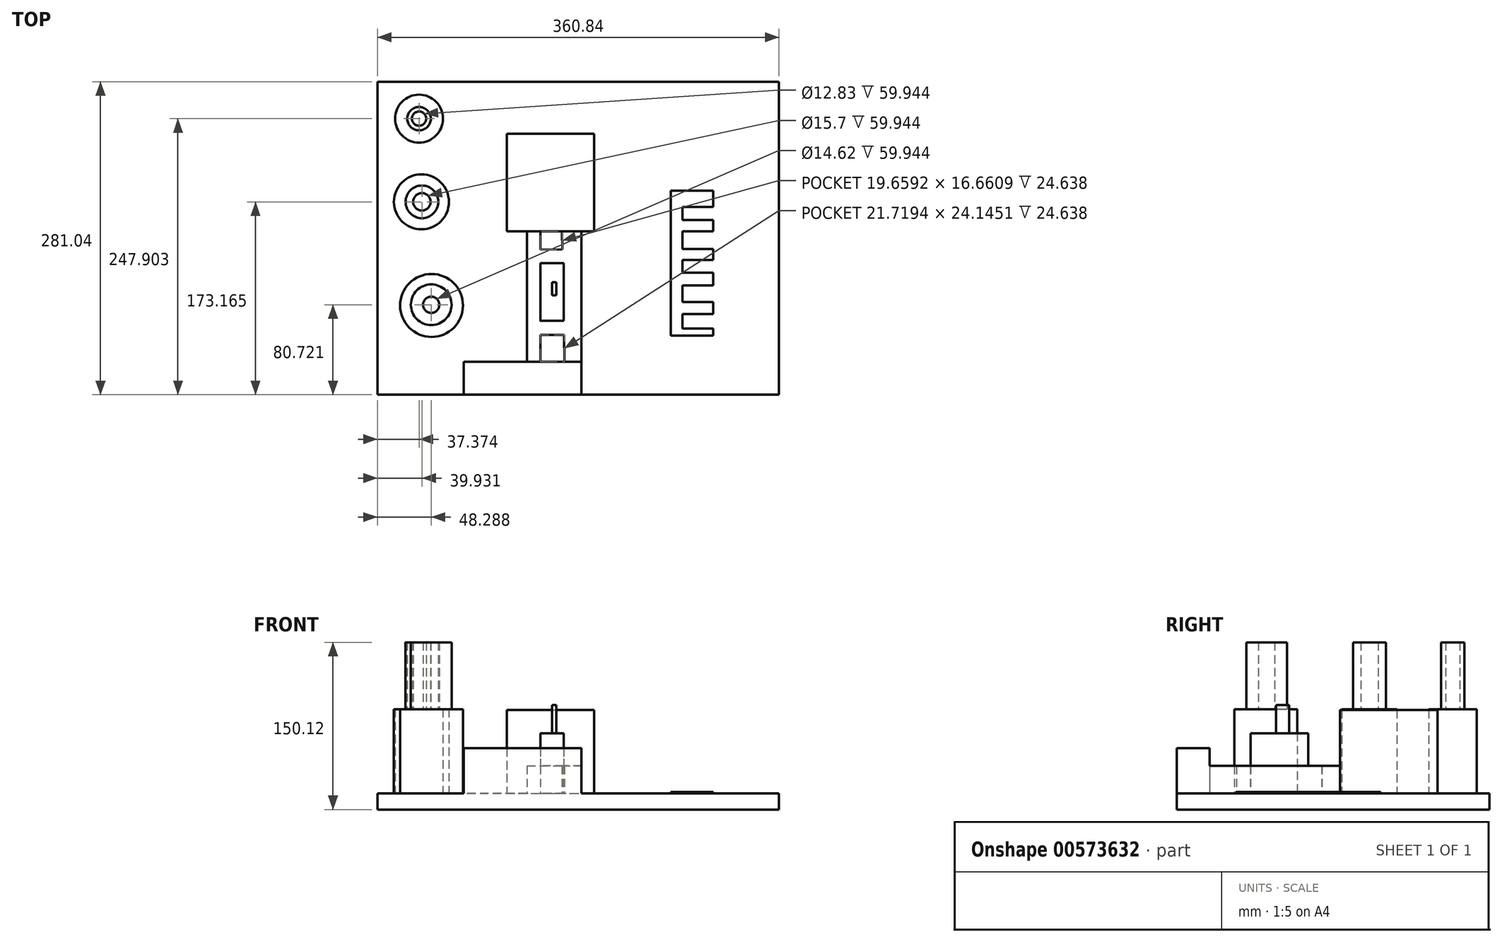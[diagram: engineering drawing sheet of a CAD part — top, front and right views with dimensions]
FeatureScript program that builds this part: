
annotation { "Feature Type Name" : "Feature", "Feature Type Description" : "" }
export const myFeature = defineFeature(function(context is Context, id is Id, definition is map)
    precondition{}
    {
        {
            var Q0;
            Q0=qCreatedBy(makeId("Top.planeOp"),FACE);
            var sketch = newSketch(context, id + "F0", { "sketchPlane" : qUnion([Q0])});
            skLineSegment(sketch, "E0.bottom", {"start": v(-194.6, 134.36) * mm, "end": v(166.24, 134.36) * mm});
            skLineSegment(sketch, "E0.top", {"start": v(-194.6, -146.68) * mm, "end": v(166.24, -146.68) * mm});
            skLineSegment(sketch, "E0.left", {"start": v(-194.6, 134.36) * mm, "end": v(-194.6, -146.68) * mm});
            skLineSegment(sketch, "E0.right", {"start": v(166.24, 134.36) * mm, "end": v(166.24, -146.68) * mm});
            skSolve(sketch);
        }
        {
            var Q0;
            Q0=makeQuery(id+"F0.imprint","IMPRINT",FACE,{"disambiguationData":[TD([[makeQuery(id+"F0.imprint","IMPRINT",EDGE,{"derivedFrom":sQuery(id+"F0.wireOp",EDGE,"E0.bottom")}),-1.0]])]});
            extrude(context, id + "F1", {"entities" : qUnion([Q0]), "oppositeDirection" : true, "depth" : 14.48 * mm, "offsetDistance" : 25.4 * mm});
        }
        {
            var Q0;
            Q0=makeQuery(id+"F1.opExtrude","CAP_FACE",FACE,{"disambiguationData":[OSD([sQuery(id+"F0.wireOp",EDGE,"E0.bottom"),sQuery(id+"F0.wireOp",EDGE,"E0.top"),sQuery(id+"F0.wireOp",EDGE,"E0.left"),sQuery(id+"F0.wireOp",EDGE,"E0.right")])],"isStart":true});
            var sketch = newSketch(context, id + "F2", { "sketchPlane" : qUnion([Q0])});
            skCircle(sketch, "E1", {"center": v(-157.23, 101.22) * mm, "radius": 21.51 * mm});
            skCircle(sketch, "E2", {"center": v(-155.1, 26.46) * mm, "radius": 24.7 * mm});
            skCircle(sketch, "E3", {"center": v(-145.98, -66.55) * mm, "radius": 28.25 * mm});
            skSolve(sketch);
        }
        {
            var Q0;
            Q0 = qSketchRegion(id + "F2", true);
            extrude(context, id + "F3", {"entities" : qUnion([Q0]), "operationType" : NewBodyOperationType.ADD, "depth" : 75.7 * mm, "offsetDistance" : 25.4 * mm});
        }
        {
            var Q0;
            Q0=makeQuery(id+"F3.opExtrude","CAP_FACE",FACE,{"disambiguationData":[OSD([sQuery(id+"F2.wireOp",EDGE,"E1")])],"isStart":false});
            var sketch = newSketch(context, id + "F4", { "sketchPlane" : qUnion([Q0])});
            skCircle(sketch, "E4", {"center": v(-157.23, 101.22) * mm, "radius": 10.56 * mm});
            skCircle(sketch, "E5", {"center": v(-154.67, 26.48) * mm, "radius": 14.66 * mm});
            skCircle(sketch, "E6", {"center": v(-146.31, -65.96) * mm, "radius": 18.29 * mm});
            skCircle(sketch, "E7", {"center": v(-146.31, -65.96) * mm, "radius": 7.31 * mm});
            skCircle(sketch, "E8", {"center": v(-154.67, 26.48) * mm, "radius": 7.85 * mm});
            skCircle(sketch, "E9", {"center": v(-157.23, 101.22) * mm, "radius": 6.41 * mm});
            skSolve(sketch);
        }
        {
            var Q0;
            Q0 = qSketchRegion(id + "F4", true);
            extrude(context, id + "F5", {"entities" : qUnion([Q0]), "operationType" : NewBodyOperationType.ADD, "depth" : 59.94 * mm, "offsetDistance" : 25.4 * mm});
        }
        {
            var Q0;
            Q0=makeQuery(id+"F1.opExtrude","CAP_FACE",FACE,{"disambiguationData":[OSD([sQuery(id+"F0.wireOp",EDGE,"E0.bottom"),sQuery(id+"F0.wireOp",EDGE,"E0.top"),sQuery(id+"F0.wireOp",EDGE,"E0.left"),sQuery(id+"F0.wireOp",EDGE,"E0.right")])],"isStart":true});
            var sketch = newSketch(context, id + "F6", { "sketchPlane" : qUnion([Q0])});
            skLineSegment(sketch, "E10.bottom", {"start": v(-78.44, 87.5) * mm, "end": v(0, 87.5) * mm});
            skLineSegment(sketch, "E10.top", {"start": v(-78.44, 0) * mm, "end": v(0, 0) * mm});
            skLineSegment(sketch, "E10.left", {"start": v(-78.44, 87.5) * mm, "end": v(-78.44, 0) * mm});
            skLineSegment(sketch, "E10.right", {"start": v(0, 87.5) * mm, "end": v(0, 0) * mm});
            skSolve(sketch);
        }
        {
            var Q0;
            Q0 = qSketchRegion(id + "F6", true);
            extrude(context, id + "F7", {"entities" : qUnion([Q0]), "operationType" : NewBodyOperationType.ADD, "depth" : 74.93 * mm, "offsetDistance" : 25.4 * mm});
        }
        {
            var Q0;
            Q0=makeQuery(id+"F1.opExtrude","CAP_FACE",FACE,{"disambiguationData":[OSD([sQuery(id+"F0.wireOp",EDGE,"E0.bottom"),sQuery(id+"F0.wireOp",EDGE,"E0.top"),sQuery(id+"F0.wireOp",EDGE,"E0.left"),sQuery(id+"F0.wireOp",EDGE,"E0.right")])],"isStart":true});
            var sketch = newSketch(context, id + "F8", { "sketchPlane" : qUnion([Q0])});
            skLineSegment(sketch, "E11", {"start": v(-60.27, 0) * mm, "end": v(-60.27, -66.73) * mm});
            skLineSegment(sketch, "E12", {"start": v(-60.27, -66.73) * mm, "end": v(-60.27, -117.28) * mm});
            skLineSegment(sketch, "E13", {"start": v(-60.27, -117.28) * mm, "end": v(-48.28, -117.28) * mm});
            skLineSegment(sketch, "E14", {"start": v(-48.28, -117.28) * mm, "end": v(-48.28, 0) * mm});
            skLineSegment(sketch, "E15", {"start": v(-48.28, 0) * mm, "end": v(-60.27, 0) * mm});
            skLineSegment(sketch, "E16", {"start": v(-28.96, 0) * mm, "end": v(-11.3, 0) * mm});
            skLineSegment(sketch, "E17", {"start": v(-11.3, 0) * mm, "end": v(-11.3, -117.28) * mm});
            skLineSegment(sketch, "E18", {"start": v(-11.3, -117.28) * mm, "end": v(-26.56, -117.28) * mm});
            skLineSegment(sketch, "E19", {"start": v(-26.56, -117.28) * mm, "end": v(-28.96, 0) * mm});
            skLineSegment(sketch, "E20", {"start": v(-48.28, -93.13) * mm, "end": v(-26.56, -93.13) * mm});
            skLineSegment(sketch, "E21", {"start": v(-26.56, -93.13) * mm, "end": v(-27.32, -80.21) * mm});
            skLineSegment(sketch, "E22", {"start": v(-27.32, -80.21) * mm, "end": v(-48.28, -80.64) * mm});
            skLineSegment(sketch, "E23", {"start": v(-48.28, -80.64) * mm, "end": v(-48.28, -93.13) * mm});
            skLineSegment(sketch, "E24", {"start": v(-48.28, -58.64) * mm, "end": v(-27.32, -58.21) * mm});
            skLineSegment(sketch, "E25", {"start": v(-27.32, -58.21) * mm, "end": v(-28.08, -42.94) * mm});
            skLineSegment(sketch, "E26", {"start": v(-28.08, -42.94) * mm, "end": v(-48.28, -43.94) * mm});
            skLineSegment(sketch, "E27", {"start": v(-48.28, -43.94) * mm, "end": v(-48.28, -58.64) * mm});
            skLineSegment(sketch, "E28", {"start": v(-48.28, -16.66) * mm, "end": v(-27.32, -16.23) * mm});
            skLineSegment(sketch, "E29", {"start": v(-27.32, -16.23) * mm, "end": v(-28.37, -28.51) * mm});
            skLineSegment(sketch, "E30", {"start": v(-28.37, -28.51) * mm, "end": v(-48.28, -28.51) * mm});
            skLineSegment(sketch, "E31", {"start": v(-48.28, -28.51) * mm, "end": v(-48.28, -16.66) * mm});
            skSolve(sketch);
        }
        {
            var Q0;
            Q0 = qSketchRegion(id + "F8", true);
            extrude(context, id + "F9", {"entities" : qUnion([Q0]), "operationType" : NewBodyOperationType.ADD, "depth" : 24.64 * mm, "offsetDistance" : 25.4 * mm});
        }
        {
            var Q0;
            {var subQ0=sQuery(id+"F8.wireOp",EDGE,"E22");Q0=makeQuery(id+"F9.boolean.opBoolean","SPLIT",FACE,{"disambiguationData":[TD([makeQuery(id+"F9.opExtrude","SWEPT_FACE",FACE,{"disambiguationData":[OSD([subQ0])]})])],"derivedFrom":makeQuery(id+"F1.opExtrude","CAP_FACE",FACE,{"disambiguationData":[OSD([sQuery(id+"F0.wireOp",EDGE,"E0.bottom"),sQuery(id+"F0.wireOp",EDGE,"E0.top"),sQuery(id+"F0.wireOp",EDGE,"E0.left"),sQuery(id+"F0.wireOp",EDGE,"E0.right")])],"isStart":true})});}
            var sketch = newSketch(context, id + "F10", { "sketchPlane" : qUnion([Q0])});
            skLineSegment(sketch, "E32.bottom", {"start": v(-48.28, -28.51) * mm, "end": v(-27.32, -28.51) * mm});
            skLineSegment(sketch, "E32.top", {"start": v(-48.28, -80.21) * mm, "end": v(-27.32, -80.21) * mm});
            skLineSegment(sketch, "E32.left", {"start": v(-48.28, -28.51) * mm, "end": v(-48.28, -80.21) * mm});
            skLineSegment(sketch, "E32.right", {"start": v(-27.32, -28.51) * mm, "end": v(-27.32, -80.21) * mm});
            skSolve(sketch);
        }
        {
            var Q0;
            Q0 = qSketchRegion(id + "F10", true);
            extrude(context, id + "F11", {"entities" : qUnion([Q0]), "operationType" : NewBodyOperationType.ADD, "depth" : 54.1 * mm, "offsetDistance" : 25.4 * mm});
        }
        {
            var Q0;
            Q0=makeQuery(id+"F11.opExtrude","CAP_FACE",FACE,{"disambiguationData":[OSD([sQuery(id+"F10.wireOp",EDGE,"E32.bottom"),sQuery(id+"F10.wireOp",EDGE,"E32.top"),sQuery(id+"F10.wireOp",EDGE,"E32.left"),sQuery(id+"F10.wireOp",EDGE,"E32.right")])],"isStart":false});
            var sketch = newSketch(context, id + "F12", { "sketchPlane" : qUnion([Q0])});
            skPoint(sketch, "E33.oppositeSnap0", {"position": v(-37.8, -80.21) * mm});
            skLineSegment(sketch, "E33.bottom", {"start": v(-34.02, -45.59) * mm, "end": v(-37.8, -45.59) * mm});
            skLineSegment(sketch, "E33.top", {"start": v(-34.02, -57.6) * mm, "end": v(-37.8, -57.6) * mm});
            skLineSegment(sketch, "E33.left", {"start": v(-34.02, -45.59) * mm, "end": v(-34.02, -57.6) * mm});
            skLineSegment(sketch, "E33.right", {"start": v(-37.8, -45.59) * mm, "end": v(-37.8, -57.6) * mm});
            skSolve(sketch);
        }
        {
            var Q0;
            Q0 = qSketchRegion(id + "F12", true);
            extrude(context, id + "F13", {"entities" : qUnion([Q0]), "operationType" : NewBodyOperationType.ADD, "depth" : 25.4 * mm, "offsetDistance" : 25.4 * mm});
        }
        {
            var Q0;
            {var subQ0=sQuery(id+"F0.wireOp",EDGE,"E0.left");var subQ2=sQuery(id+"F0.wireOp",EDGE,"E0.bottom");var subQ4=sQuery(id+"F0.wireOp",EDGE,"E0.right");var subQ5=sQuery(id+"F0.wireOp",EDGE,"E0.top");Q0=makeQuery(id+"F9.boolean.opBoolean","SPLIT",FACE,{"disambiguationData":[TD([makeQuery(id+"F1.opExtrude","SWEPT_FACE",FACE,{"disambiguationData":[OSD([subQ2])]})])],"derivedFrom":makeQuery(id+"F1.opExtrude","CAP_FACE",FACE,{"disambiguationData":[OSD([subQ2,subQ5,subQ0,subQ4])],"isStart":true})});}
            var sketch = newSketch(context, id + "F14", { "sketchPlane" : qUnion([Q0])});
            skLineSegment(sketch, "E34.bottom", {"start": v(-11.3, -117.28) * mm, "end": v(-117.06, -117.28) * mm});
            skLineSegment(sketch, "E34.top", {"start": v(-11.3, -146.68) * mm, "end": v(-117.06, -146.68) * mm});
            skLineSegment(sketch, "E34.left", {"start": v(-11.3, -117.28) * mm, "end": v(-11.3, -146.68) * mm});
            skLineSegment(sketch, "E34.right", {"start": v(-117.06, -117.28) * mm, "end": v(-117.06, -146.68) * mm});
            skSolve(sketch);
        }
        {
            var Q0;
            Q0 = qSketchRegion(id + "F14", true);
            extrude(context, id + "F15", {"entities" : qUnion([Q0]), "operationType" : NewBodyOperationType.ADD, "depth" : 40.64 * mm, "offsetDistance" : 25.4 * mm});
        }
        {
            var Q0;
            {var subQ3=sQuery(id+"F0.wireOp",EDGE,"E0.left");var subQ7=sQuery(id+"F0.wireOp",EDGE,"E0.bottom");var subQ8=makeQuery(id+"F1.opExtrude","SWEPT_FACE",FACE,{"disambiguationData":[OSD([subQ7])]});var subQ9=sQuery(id+"F0.wireOp",EDGE,"E0.right");var subQ11=sQuery(id+"F0.wireOp",EDGE,"E0.top");Q0=makeQuery(id+"F15.boolean.opBoolean","SPLIT",FACE,{"disambiguationData":[TD([subQ8])],"derivedFrom":makeQuery(id+"F9.boolean.opBoolean","SPLIT",FACE,{"disambiguationData":[TD([subQ8])],"derivedFrom":makeQuery(id+"F1.opExtrude","CAP_FACE",FACE,{"disambiguationData":[OSD([subQ7,subQ11,subQ3,subQ9])],"isStart":true})})});}
            var sketch = newSketch(context, id + "F16", { "sketchPlane" : qUnion([Q0])});
            skLineSegment(sketch, "E35", {"start": v(68.87, 36.4) * mm, "end": v(68.87, -93.64) * mm});
            skLineSegment(sketch, "E36", {"start": v(68.87, -93.64) * mm, "end": v(107, -93.64) * mm});
            skLineSegment(sketch, "E37", {"start": v(107, -93.64) * mm, "end": v(107, -87.37) * mm});
            skLineSegment(sketch, "E38", {"start": v(107, -87.37) * mm, "end": v(79.31, -87.37) * mm});
            skLineSegment(sketch, "E39", {"start": v(79.31, -87.37) * mm, "end": v(79.31, -74.32) * mm});
            skLineSegment(sketch, "E40", {"start": v(79.31, -74.32) * mm, "end": v(107, -74.32) * mm});
            skLineSegment(sketch, "E41", {"start": v(107, -74.32) * mm, "end": v(107, -63.35) * mm});
            skLineSegment(sketch, "E42", {"start": v(107, -63.35) * mm, "end": v(79.31, -63.35) * mm});
            skLineSegment(sketch, "E43", {"start": v(79.31, -63.35) * mm, "end": v(79.31, -48.72) * mm});
            skLineSegment(sketch, "E44", {"start": v(79.31, -48.72) * mm, "end": v(107, -48.72) * mm});
            skLineSegment(sketch, "E45", {"start": v(107, -48.72) * mm, "end": v(107, -37.23) * mm});
            skLineSegment(sketch, "E46", {"start": v(107, -37.23) * mm, "end": v(79.31, -37.23) * mm});
            skLineSegment(sketch, "E47", {"start": v(79.31, -37.23) * mm, "end": v(79.31, -25.74) * mm});
            skLineSegment(sketch, "E48", {"start": v(79.31, -25.74) * mm, "end": v(107, -25.74) * mm});
            skLineSegment(sketch, "E49", {"start": v(107, -25.74) * mm, "end": v(107, -15.82) * mm});
            skLineSegment(sketch, "E50", {"start": v(107, -15.82) * mm, "end": v(79.31, -15.82) * mm});
            skLineSegment(sketch, "E51", {"start": v(79.31, -15.82) * mm, "end": v(79.31, 0) * mm});
            skLineSegment(sketch, "E52", {"start": v(79.31, 0) * mm, "end": v(107, 0) * mm});
            skLineSegment(sketch, "E53", {"start": v(107, 0) * mm, "end": v(107, 10.3) * mm});
            skLineSegment(sketch, "E54", {"start": v(107, 10.3) * mm, "end": v(79.31, 10.3) * mm});
            skLineSegment(sketch, "E55", {"start": v(79.31, 10.3) * mm, "end": v(79.31, 21.78) * mm});
            skLineSegment(sketch, "E56", {"start": v(79.31, 21.78) * mm, "end": v(107, 21.78) * mm});
            skLineSegment(sketch, "E57", {"start": v(107, 21.78) * mm, "end": v(107, 36.4) * mm});
            skLineSegment(sketch, "E58", {"start": v(107, 36.4) * mm, "end": v(68.87, 36.4) * mm});
            skSolve(sketch);
        }
        {
            var Q0;
            Q0 = qSketchRegion(id + "F16", true);
            extrude(context, id + "F17", {"entities" : qUnion([Q0]), "operationType" : NewBodyOperationType.ADD, "depth" : 1.27 * mm, "offsetDistance" : 25.4 * mm});
        }
    });
